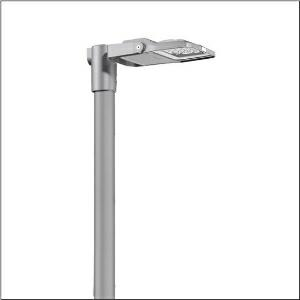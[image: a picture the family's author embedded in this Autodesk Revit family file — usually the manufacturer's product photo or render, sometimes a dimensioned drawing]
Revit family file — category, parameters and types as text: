
# Revit family: floodlight_fl_21_iq_micro___pl33t_5xa7761a2f3a_d57c
name_source: partatom
category: Lighting Fixtures
units: mm (PartAtom-declared; Revit-internal decimal feet)

## family parameters
Cut with Voids When Loaded = No
Host = Face
Light Source = No
Part Type = Normal
Room Calculation Point = No
Round Connector Dimension = Use Diameter
Shared = No

## types (1)
- --- (1 x LED, 2930 lm, 23.1 W, 3000K)
    Apparent Load = 23 VA
    CIE Flux Codes = 26 75 99 100 100
    Color Rendering = 70
    Color Temperature = 3000K
    Default Elevation = 1800 mm
    Description = Floodlight FL 21 iQ micro, floodlight, primary light control with lens, of PMMA, primary optical cover: protective disc, of toughened safety glass, transparent, light distribution: PL33T, light emission: direct distribution, installation type: surface-mounted, LED, High Power LED, rated luminous flux: 2.930lm, luminous efficacy: 127lm/W, light colour: 730, colour temperature: 3000K, control gear: iQ Comfort/DALI, control: optimised constant luminous flux control (CLO 2.0), Desk-Remote (wireless, voltage-free reading and setting of iQ features in the workshop via application-optimized NFC function/RFID function), Light-Fading, Smart-Wire, Night-Set, Lumen-Switch, Temp-Guard, Auto-Match, with terminal, 6-pole, mains connection: 220..240V, AC, 50/60Hz, start of lifetime: 23W, end of service life: 24W, reduction: 11W, luminaire housing, of diecast aluminium, powder-coated, Siteco® metallic grey (DB 702S), corrosivity category C5 mid according to DIN EN ISO 12944, suitable for swimming pools, chlorine-resistant, sealing non-destructively replaceable, please order mast flange separately, mast bracket, of steel, galvanised, powder-coated, Siteco® metallic grey (DB 702S), protection rating (complete): IP66, insulation class (complete): insulation class II (safety insulation), certification: CE, ENEC, VDE, protection symbol: D, impact resistance: IK07, permissible operating ambient temperature: -40..+40°C, permissible operating ambient temperature for outdoor applications: -40..+50°C, standard: DIN EN 12944, LABS conformity tested according to VDMA 24364:2018-05, packaging unit: 1 piece

Light Distribution: PL33T
    Height = 65 mm
    Lamp = 1 x LED
    Lamp Light Flux = 2930 lm
    Lamp Power = 23.1 W
    Lamp count = 1
    Length = 312 mm
    Luminous efficacy = 127 lm/W
    Manufacturer = Siteco
    ModVariant = No
    Model = 5XA7761A2F3A
    Number of Poles = 1
    OnlyDefault = Yes
    Power Factor = 1
    Product Name = Floodlight FL 21 iQ micro | PL33T
    Product group = floodlight | pylon top
    ProductGroupID = 6101
    Protection Class = Protection class II
    Protection Degree = IP 66
    RLX_Detail_Level = 1
    RLX_Emergency_Light_Flux = 0 lm
    RLX_Emergency_Type = 0
    RLX_Emergency_Type_DB = No
    RlxData = <blob elided: 101689 chars, md5=6cace1a0>
    Socket = socket
    Standby Power = 0 W
    System Light Flux = 2930 lm
    System Power = 23 W
    Type Comments = factory setting: luminous flux: 100 % | dim-lin: 254 | 455 mA
    Type Image = l_1007121.jpg
    URL = http://relux.com
    VarID = @adj_148226
    Voltage = 0 V
    Weight = 0.00 kg
    Width = 230 mm

## geometry (parser evidence)
native form markers: Blend x4, Sweep x12
no freeform markers — native parametric forms only
